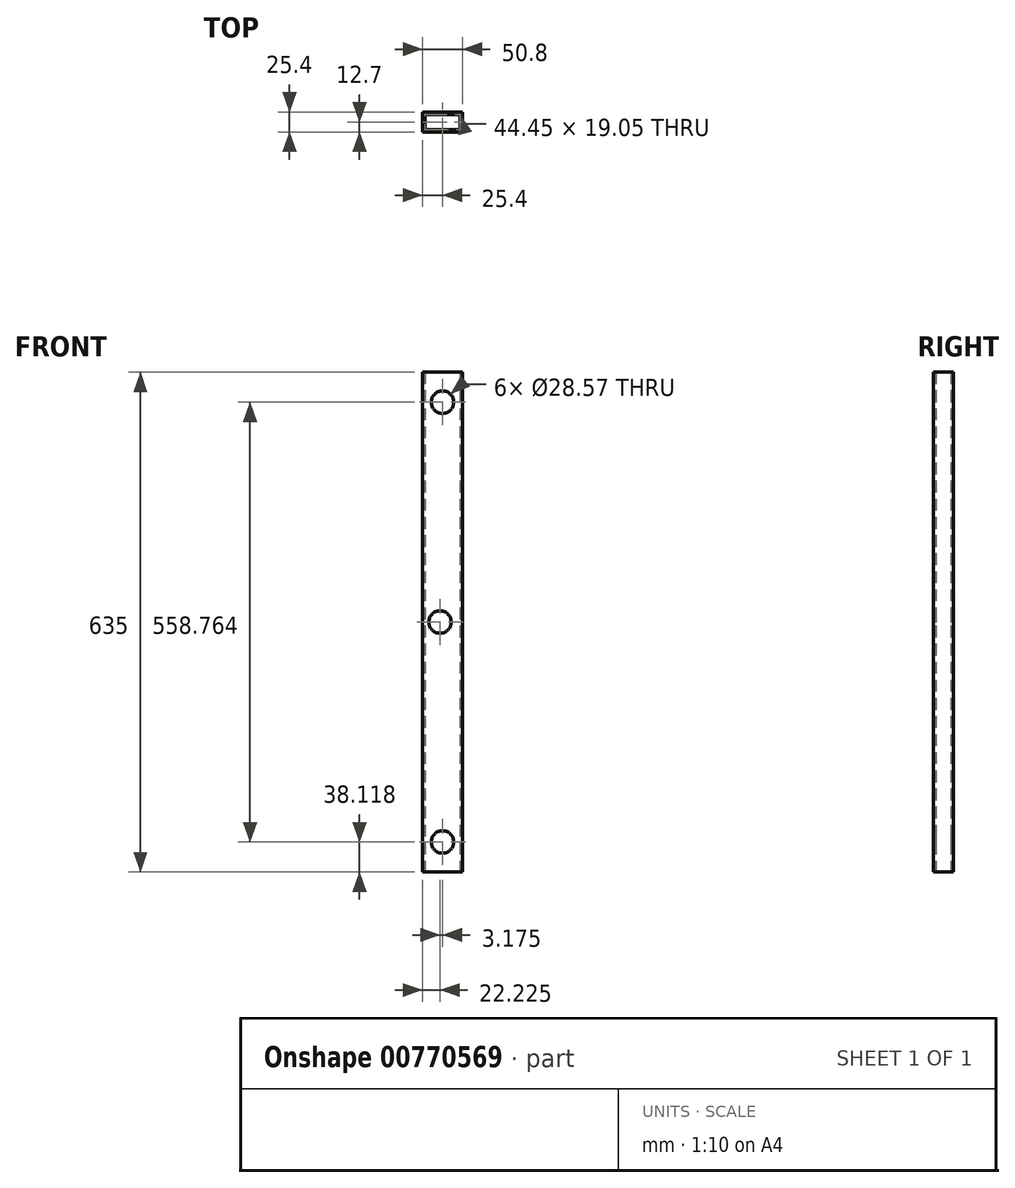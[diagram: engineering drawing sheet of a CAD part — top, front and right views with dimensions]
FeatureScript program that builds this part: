
annotation { "Feature Type Name" : "Feature", "Feature Type Description" : "" }
export const myFeature = defineFeature(function(context is Context, id is Id, definition is map)
    precondition{}
    {
        {
            var Q0;
            Q0=qCreatedBy(makeId("Top.planeOp"),FACE);
            var sketch = newSketch(context, id + "F0", { "sketchPlane" : qUnion([Q0])});
            skLineSegment(sketch, "E0", {"start": v(0, 0) * mm, "end": v(0, 25.4) * mm});
            skLineSegment(sketch, "E1", {"start": v(0, 25.4) * mm, "end": v(50.8, 25.4) * mm});
            skLineSegment(sketch, "E2", {"start": v(50.8, 25.4) * mm, "end": v(50.8, 0) * mm});
            skLineSegment(sketch, "E3", {"start": v(50.8, 0) * mm, "end": v(0, 0) * mm});
            skLineSegment(sketch, "E4.bottom", {"start": v(3.18, 22.22) * mm, "end": v(47.62, 22.23) * mm});
            skLineSegment(sketch, "E4.top", {"start": v(3.17, 3.17) * mm, "end": v(47.62, 3.18) * mm});
            skLineSegment(sketch, "E4.left", {"start": v(3.17, 22.23) * mm, "end": v(3.17, 3.17) * mm});
            skLineSegment(sketch, "E4.right", {"start": v(47.62, 22.23) * mm, "end": v(47.62, 3.17) * mm});
            skPoint(sketch, "E4.middle", {"position": v(25.4, 12.7) * mm});
            skLineSegment(sketch, "E5", {"start": v(25.4, 25.4) * mm, "end": v(25.4, 22.23) * mm, "construction": true});
            skLineSegment(sketch, "E6", {"start": v(0, 12.7) * mm, "end": v(3.17, 12.7) * mm, "construction": true});
            skPoint(sketch, "E6.endSnap0", {"position": v(3.17, 12.7) * mm});
            skSolve(sketch);
        }
        {
            var Q0;
            Q0 = qSketchRegion(id + "F0", true);
            extrude(context, id + "F1", {"entities" : qUnion([Q0]), "depth" : 635 * mm, "offsetDistance" : 25.4 * mm});
        }
        {
            var Q0;
            Q0=makeQuery(id+"F1.opExtrude","SWEPT_FACE",FACE,{"disambiguationData":[OSD([sQuery(id+"F0.wireOp",EDGE,"E1")])]});
            var sketch = newSketch(context, id + "F2", { "sketchPlane" : qUnion([Q0])});
            skLineSegment(sketch, "E7", {"start": v(-25.4, 38.12) * mm, "end": v(-22.23, 317.5) * mm, "construction": true});
            skLineSegment(sketch, "E8", {"start": v(-22.23, 317.5) * mm, "end": v(-25.4, 596.88) * mm, "construction": true});
            skLineSegment(sketch, "E9", {"start": v(-25.4, 596.88) * mm, "end": v(-25.4, 38.12) * mm, "construction": true});
            skLineSegment(sketch, "E10", {"start": v(-25.4, 317.5) * mm, "end": v(-50.8, 317.5) * mm, "construction": true});
            skCircle(sketch, "E11", {"center": v(-25.4, 596.88) * mm, "radius": 14.29 * mm});
            skCircle(sketch, "E12", {"center": v(-22.23, 317.5) * mm, "radius": 14.29 * mm});
            skCircle(sketch, "E13", {"center": v(-25.4, 38.12) * mm, "radius": 14.29 * mm});
            skSolve(sketch);
        }
        {
            var Q0;
            Q0 = qSketchRegion(id + "F2", true);
            extrude(context, id + "F3", {"entities" : qUnion([Q0]), "operationType" : NewBodyOperationType.REMOVE, "endBound" : BoundingType.THROUGH_ALL, "oppositeDirection" : true, "depth" : 25.4 * mm, "offsetDistance" : 25.4 * mm});
        }
    });
